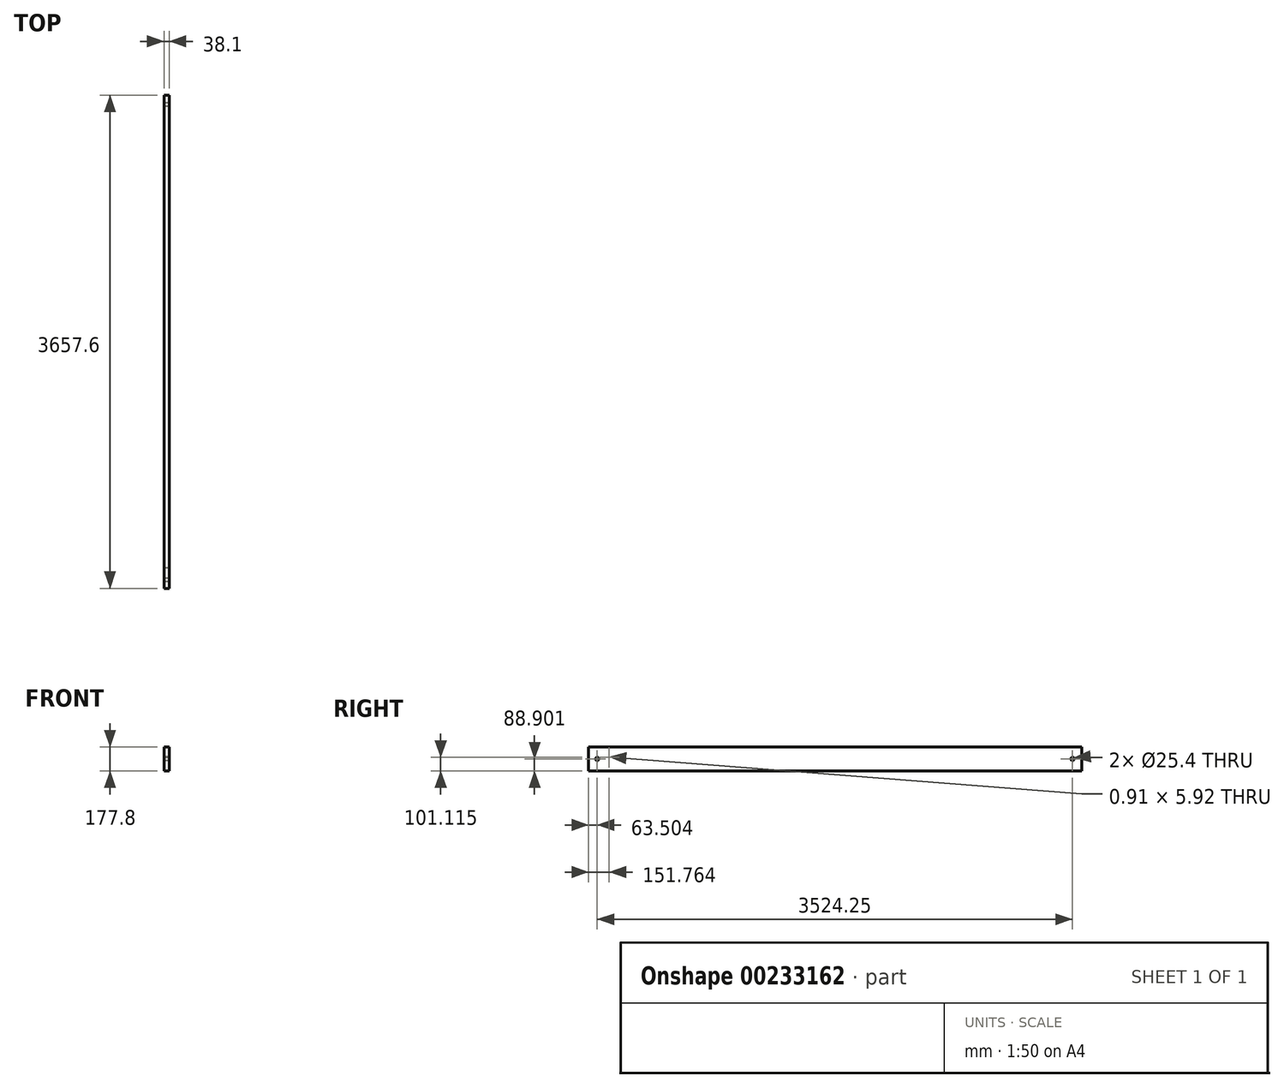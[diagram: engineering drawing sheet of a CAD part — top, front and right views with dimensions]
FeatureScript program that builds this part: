
annotation { "Feature Type Name" : "Feature", "Feature Type Description" : "" }
export const myFeature = defineFeature(function(context is Context, id is Id, definition is map)
    precondition{}
    {
        {
            var Q0;
            Q0=qCreatedBy(makeId("Right.planeOp"),FACE);
            var sketch = newSketch(context, id + "F0", { "sketchPlane" : qUnion([Q0])});
            skLineSegment(sketch, "E0.bottom", {"start": v(-230.97, 189.6) * mm, "end": v(3426.63, 189.6) * mm});
            skLineSegment(sketch, "E0.top", {"start": v(-230.97, 11.8) * mm, "end": v(3426.63, 11.8) * mm});
            skLineSegment(sketch, "E0.left", {"start": v(-230.97, 189.6) * mm, "end": v(-230.97, 11.8) * mm});
            skLineSegment(sketch, "E0.right", {"start": v(3426.63, 189.6) * mm, "end": v(3426.63, 11.8) * mm});
            skLineSegment(sketch, "E1.bottom", {"start": v(-78.75, 109.94) * mm, "end": v(-79.66, 109.94) * mm});
            skLineSegment(sketch, "E1.top", {"start": v(-78.75, 115.87) * mm, "end": v(-79.66, 115.87) * mm});
            skLineSegment(sketch, "E1.left", {"start": v(-78.75, 109.94) * mm, "end": v(-78.75, 115.87) * mm});
            skLineSegment(sketch, "E1.right", {"start": v(-79.66, 109.94) * mm, "end": v(-79.66, 115.87) * mm});
            skCircle(sketch, "E2", {"center": v(3356.78, 100.7) * mm, "radius": 12.7 * mm});
            skCircle(sketch, "E3", {"center": v(-167.47, 100.7) * mm, "radius": 12.7 * mm});
            skSolve(sketch);
        }
        {
            var Q0;
            Q0=makeQuery(id+"F0.imprint","IMPRINT",FACE,{"disambiguationData":[TD([[makeQuery(id+"F0.imprint","IMPRINT",EDGE,{"derivedFrom":sQuery(id+"F0.wireOp",EDGE,"E0.bottom")}),-1.0]])]});
            extrude(context, id + "F1", {"entities" : qUnion([Q0]), "depth" : 38.1 * mm});
        }
    });
